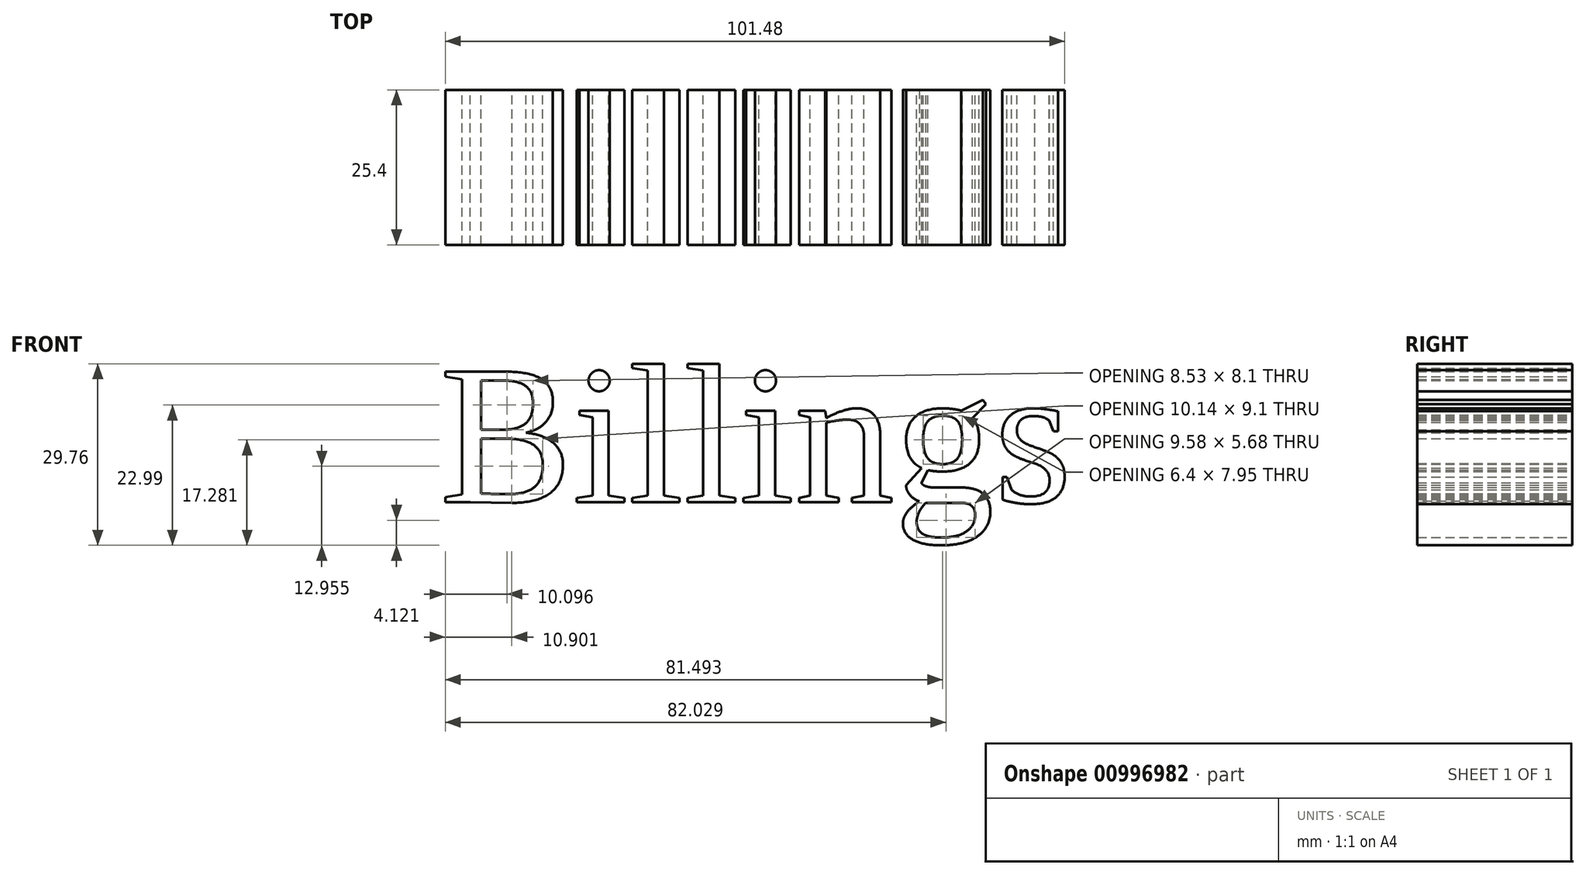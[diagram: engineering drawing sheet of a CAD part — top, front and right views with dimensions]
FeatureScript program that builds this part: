
annotation { "Feature Type Name" : "Feature", "Feature Type Description" : "" }
export const myFeature = defineFeature(function(context is Context, id is Id, definition is map)
    precondition{}
    {
        {
            var Q0;
            Q0=qCreatedBy(makeId("Front.planeOp"),FACE);
            var sketch = newSketch(context, id + "F0", { "sketchPlane" : qUnion([Q0])});
            skText(sketch, "E0", { "text": "Billings", "fontName": "Tinos-Regular.ttf"});
            const initialGuessF0  = {"E0": [-0.0417, 0.0402, 1, 0, 0.02355]};
            skSetInitialGuess(sketch, initialGuessF0);
            skSolve(sketch);
        }
        {
            var Q0;
            Q0 = qSketchRegion(id + "F0", true);
            extrude(context, id + "F1", {"entities" : qUnion([Q0]), "depth" : 25.4 * mm, "offsetDistance" : 25.4 * mm});
        }
    });
